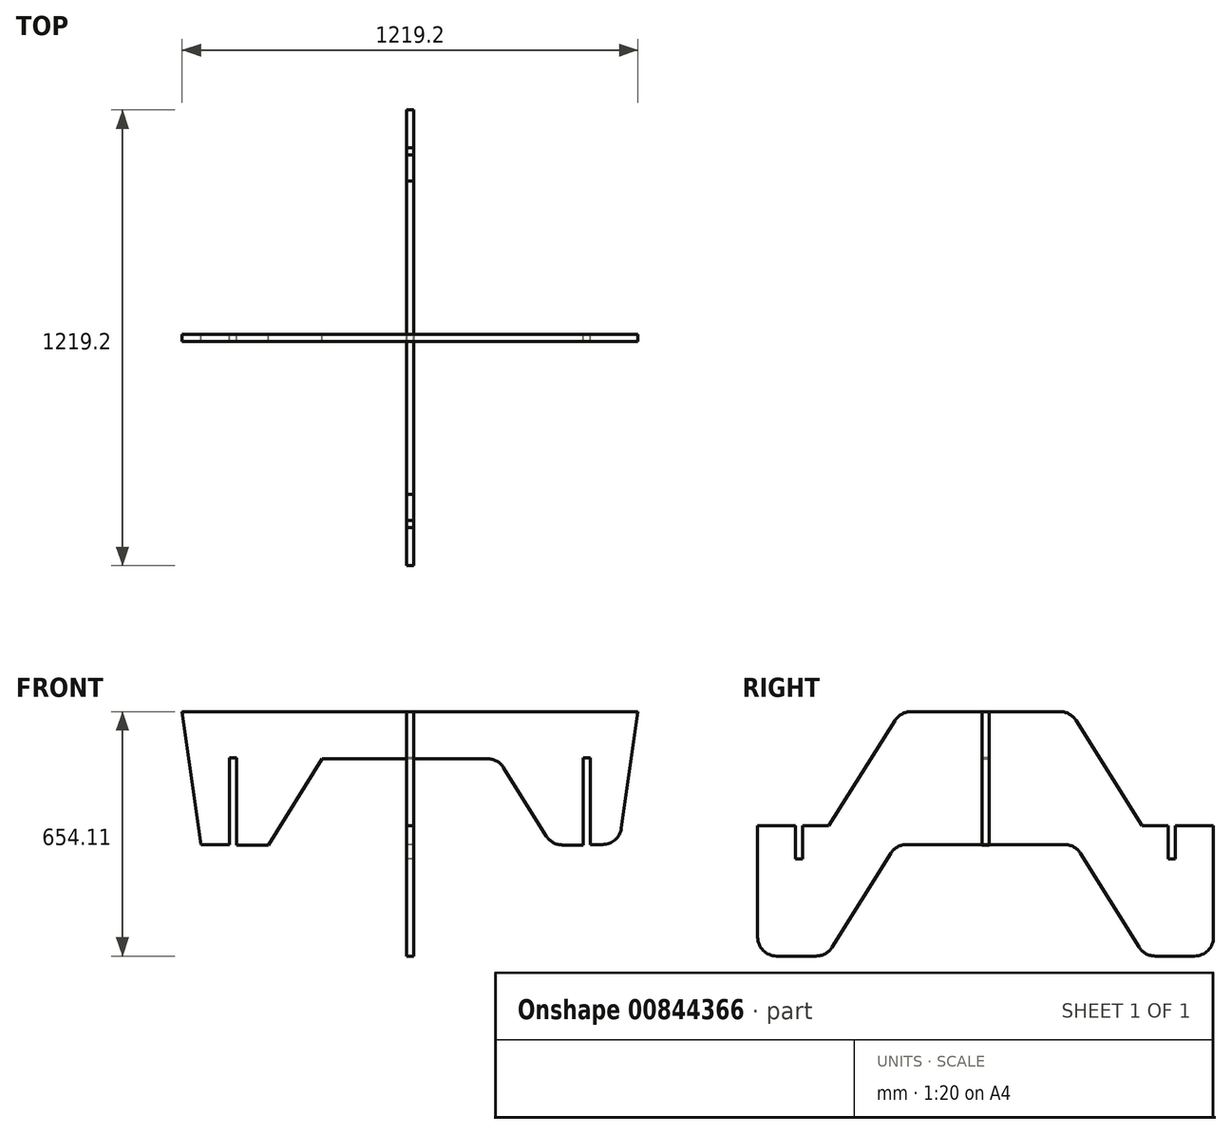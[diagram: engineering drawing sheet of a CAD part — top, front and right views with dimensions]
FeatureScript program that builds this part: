
annotation { "Feature Type Name" : "Feature", "Feature Type Description" : "" }
export const myFeature = defineFeature(function(context is Context, id is Id, definition is map)
    precondition{}
    {
        {
            var Q0;
            Q0=qCreatedBy(makeId("Front.planeOp"),FACE);
            var sketch = newSketch(context, id + "F0", { "sketchPlane" : qUnion([Q0])});
            skLineSegment(sketch, "E0", {"start": v(0, 0) * mm, "end": v(609.6, 0) * mm});
            skLineSegment(sketch, "E1", {"start": v(609.6, 0) * mm, "end": v(565.03, -311.98) * mm});
            skLineSegment(sketch, "E2.bottom", {"start": v(463.55, -123.83) * mm, "end": v(482.6, -123.83) * mm});
            skLineSegment(sketch, "E2.left", {"start": v(463.55, -123.83) * mm, "end": v(463.55, -356.92) * mm});
            skLineSegment(sketch, "E2.right", {"start": v(482.6, -123.83) * mm, "end": v(482.6, -355.6) * mm});
            skPoint(sketch, "E3", {"position": v(482.6, 0) * mm});
            skLineSegment(sketch, "E4", {"start": v(482.6, -355.6) * mm, "end": v(514.74, -355.6) * mm});
            skLineSegment(sketch, "E5", {"start": v(0, -126.02) * mm, "end": v(206.8, -126.02) * mm});
            skLineSegment(sketch, "E6", {"start": v(249.87, -149.9) * mm, "end": v(364.31, -333.04) * mm});
            skLineSegment(sketch, "E7", {"start": v(407.4, -356.92) * mm, "end": v(463.55, -356.92) * mm});
            skLineSegment(sketch, "E8.MirrorCS", {"start": v(-609.6, 0) * mm, "end": v(-558.8, -355.6) * mm});
            skLineSegment(sketch, "E9.MirrorCS", {"start": v(-482.6, -355.6) * mm, "end": v(-558.8, -355.6) * mm});
            skLineSegment(sketch, "E10.MirrorCS", {"start": v(-482.6, -123.83) * mm, "end": v(-482.6, -355.6) * mm});
            skLineSegment(sketch, "E11.MirrorCS", {"start": v(-463.55, -123.83) * mm, "end": v(-482.6, -123.83) * mm});
            skLineSegment(sketch, "E12.MirrorCS", {"start": v(-463.55, -123.83) * mm, "end": v(-463.55, -356.92) * mm});
            skLineSegment(sketch, "E13.MirrorCS", {"start": v(-379.23, -356.92) * mm, "end": v(-463.55, -356.92) * mm});
            skLineSegment(sketch, "E14.MirrorCS", {"start": v(-234.95, -126.02) * mm, "end": v(-379.23, -356.92) * mm});
            skLineSegment(sketch, "E15.MirrorCS", {"start": v(0, 0) * mm, "end": v(-609.6, 0) * mm});
            skLineSegment(sketch, "E16.MirrorCS", {"start": v(0, -126.02) * mm, "end": v(-234.95, -126.02) * mm});
            skPoint(sketch, "E17.visualSharp", {"position": v(234.95, -126.02) * mm});
            skArc(sketch, "E17.filletArc", {"start": v(249.87, -149.9) * mm, "mid": v(231.42, -132.4) * mm, "end": v(206.8, -126.02) * mm});
            skPoint(sketch, "E18.visualSharp", {"position": v(379.23, -356.92) * mm});
            skArc(sketch, "E18.filletArc", {"start": v(364.31, -333.04) * mm, "mid": v(382.76, -350.55) * mm, "end": v(407.4, -356.92) * mm});
            skPoint(sketch, "E19.visualSharp", {"position": v(558.8, -355.6) * mm});
            skArc(sketch, "E19.filletArc", {"start": v(514.74, -355.6) * mm, "mid": v(548.03, -343.18) * mm, "end": v(565.03, -311.98) * mm});
            skSolve(sketch);
        }
        {
            var Q0;
            Q0=qCreatedBy(makeId("Right.planeOp"),FACE);
            var sketch = newSketch(context, id + "F1", { "sketchPlane" : qUnion([Q0])});
            skLineSegment(sketch, "E20", {"start": v(-609.6, -304.86) * mm, "end": v(-609.6, -603.31) * mm});
            skLineSegment(sketch, "E21", {"start": v(-558.8, -654.11) * mm, "end": v(-453.6, -654.11) * mm});
            skPoint(sketch, "E22.endSnap0", {"position": v(-3.97, -355.6) * mm});
            skLineSegment(sketch, "E23", {"start": v(-210.76, -355.6) * mm, "end": v(-3.97, -355.6) * mm});
            skLineSegment(sketch, "E24", {"start": v(-410.53, -630.23) * mm, "end": v(-253.84, -379.48) * mm});
            skLineSegment(sketch, "E25", {"start": v(-609.6, -304.86) * mm, "end": v(-508, -304.86) * mm});
            skPoint(sketch, "E26", {"position": v(-226.81, 0) * mm});
            skLineSegment(sketch, "E27", {"start": v(-419.1, -304.86) * mm, "end": v(-241.76, -23.7) * mm});
            skLineSegment(sketch, "E28.top", {"start": v(-508, -393.76) * mm, "end": v(-488.95, -393.76) * mm});
            skLineSegment(sketch, "E28.left", {"start": v(-508, -304.86) * mm, "end": v(-508, -393.76) * mm});
            skLineSegment(sketch, "E28.right", {"start": v(-488.95, -304.86) * mm, "end": v(-488.95, -393.76) * mm});
            skLineSegment(sketch, "E29", {"start": v(-198.8, 0) * mm, "end": v(-9.84, 0) * mm});
            skLineSegment(sketch, "E30.trimOffspring", {"start": v(-488.95, -304.86) * mm, "end": v(-419.1, -304.86) * mm});
            skPoint(sketch, "E31", {"position": v(-609.6, 0) * mm});
            skPoint(sketch, "E32", {"position": v(0, -654.11) * mm});
            skPoint(sketch, "E33.visualSharp", {"position": v(-238.92, -355.6) * mm});
            skArc(sketch, "E33.filletArc", {"start": v(-210.76, -355.6) * mm, "mid": v(-235.39, -361.97) * mm, "end": v(-253.84, -379.48) * mm});
            skPoint(sketch, "E34.visualSharp", {"position": v(-425.45, -654.11) * mm});
            skArc(sketch, "E34.filletArc", {"start": v(-453.6, -654.11) * mm, "mid": v(-428.98, -647.74) * mm, "end": v(-410.53, -630.23) * mm});
            skPoint(sketch, "E35.visualSharp", {"position": v(-609.6, -654.11) * mm});
            skArc(sketch, "E35.filletArc", {"start": v(-609.6, -603.31) * mm, "mid": v(-594.72, -639.23) * mm, "end": v(-558.8, -654.11) * mm});
            skArc(sketch, "E36.filletArc", {"start": v(-198.8, 0) * mm, "mid": v(-223.33, -6.32) * mm, "end": v(-241.76, -23.7) * mm});
            skLineSegment(sketch, "E37", {"start": v(-9.84, 0) * mm, "end": v(-9.84, -123.83) * mm});
            skLineSegment(sketch, "E38", {"start": v(-9.84, -123.83) * mm, "end": v(0, -123.83) * mm});
            skLineSegment(sketch, "E39.MirrorCS", {"start": v(508, -393.76) * mm, "end": v(488.95, -393.76) * mm});
            skLineSegment(sketch, "E40.MirrorCS", {"start": v(9.84, -123.83) * mm, "end": v(0, -123.83) * mm});
            skPoint(sketch, "E41.MirrorP", {"position": v(226.81, 0) * mm});
            skArc(sketch, "E42.MirrorCS", {"start": v(453.6, -654.11) * mm, "mid": v(428.98, -647.74) * mm, "end": v(410.53, -630.23) * mm});
            skArc(sketch, "E43.MirrorCS", {"start": v(210.76, -355.6) * mm, "mid": v(235.39, -361.97) * mm, "end": v(253.84, -379.48) * mm});
            skLineSegment(sketch, "E44.MirrorCS", {"start": v(488.95, -304.86) * mm, "end": v(419.1, -304.86) * mm});
            skLineSegment(sketch, "E45.MirrorCS", {"start": v(198.8, 0) * mm, "end": v(9.84, 0) * mm});
            skLineSegment(sketch, "E46.MirrorCS", {"start": v(488.95, -304.86) * mm, "end": v(488.95, -393.76) * mm});
            skLineSegment(sketch, "E47.MirrorCS", {"start": v(508, -304.86) * mm, "end": v(508, -393.76) * mm});
            skLineSegment(sketch, "E48.MirrorCS", {"start": v(419.1, -304.86) * mm, "end": v(241.76, -23.7) * mm});
            skLineSegment(sketch, "E49.MirrorCS", {"start": v(609.6, -304.86) * mm, "end": v(508, -304.86) * mm});
            skLineSegment(sketch, "E50.MirrorCS", {"start": v(410.53, -630.23) * mm, "end": v(253.84, -379.48) * mm});
            skLineSegment(sketch, "E51.MirrorCS", {"start": v(210.76, -355.6) * mm, "end": v(3.97, -355.6) * mm});
            skLineSegment(sketch, "E52.MirrorCS", {"start": v(558.8, -654.11) * mm, "end": v(453.6, -654.11) * mm});
            skLineSegment(sketch, "E53.MirrorCS", {"start": v(609.6, -304.86) * mm, "end": v(609.6, -603.31) * mm});
            skArc(sketch, "E54.MirrorCS", {"start": v(198.8, 0) * mm, "mid": v(223.33, -6.32) * mm, "end": v(241.76, -23.7) * mm});
            skArc(sketch, "E55.MirrorCS", {"start": v(609.6, -603.31) * mm, "mid": v(594.72, -639.23) * mm, "end": v(558.8, -654.11) * mm});
            skPoint(sketch, "E56.MirrorP", {"position": v(3.97, -355.6) * mm});
            skLineSegment(sketch, "E57.MirrorCS", {"start": v(9.84, 0) * mm, "end": v(9.84, -123.83) * mm});
            skPoint(sketch, "E58.MirrorP", {"position": v(609.6, 0) * mm});
            skPoint(sketch, "E59.MirrorP", {"position": v(238.92, -355.6) * mm});
            skPoint(sketch, "E60.MirrorP", {"position": v(425.45, -654.11) * mm});
            skPoint(sketch, "E61.MirrorP", {"position": v(609.6, -654.11) * mm});
            skLineSegment(sketch, "E62", {"start": v(-3.97, -355.6) * mm, "end": v(3.97, -355.6) * mm});
            skSolve(sketch);
        }
        {
            var Q0;
            Q0 = qSketchRegion(id + "F1", true);
            extrude(context, id + "F2", {"entities" : qUnion([Q0]), "endBound" : BoundingType.SYMMETRIC, "depth" : 19.05 * mm, "offsetDistance" : 25.4 * mm});
        }
        {
            var Q0;
            Q0=makeQuery(id+"F0.imprint","IMPRINT",FACE,{"disambiguationData":[TD([[makeQuery(id+"F0.imprint","IMPRINT",EDGE,{"derivedFrom":sQuery(id+"F0.wireOp",EDGE,"E0")}),-1.0]])]});
            extrude(context, id + "F3", {"entities" : qUnion([Q0]), "endBound" : BoundingType.SYMMETRIC, "depth" : 19.05 * mm, "offsetDistance" : 25.4 * mm});
        }
    });
